# Revit family: DN2_2.0_RT_EC_1FP
name_source: partatom
category: Mechanical Equipment
units: mm (PartAtom-declared; Revit-internal decimal feet)

## family parameters
Always vertical = Yes
Cut with Voids When Loaded = No
OmniClass Number = 23.75.00.00
OmniClass Title = Climate Control (HVAC)
Part Type = Normal
Room Calculation Point = No
Round Connector Dimension = Use Diameter
Shared = No
Work Plane-Based = No

## types (6) — shared parameters
Available Options = Fixed Speed Compressor, Suction Accumlator w/HGRH, Modulating 3-way Valve w/HGRH
Description = Energy Recovery Ventilator
Features (default) = BLDC Variable Speed Compressor, Integrated Refrigeration Controller, Electronic Expansion Valve, Filter Drier, Sight Glass
Manufacturer = Renewaire LLC
Model = DN-2RT-1FP-EC
Nominal Capacity Range = 2T - 10T
Number of Condenser Fans = Qty. 1, EC motor, Direct drive
Refrigerant = R410A
Typical Airflow Range = 375-1,650 CFM
URL = www.renewaire.com

## type names (no varying parameters)
- 2 @ 1.35 kW ea.
- 2 @ 2.70 kW ea.
- 2 @ 3.70 kW ea.
- 2 @ 3HP ea. 208-230V
- 2 @ 3HP ea. 460V
- 2 @ 3HP ea. 575V

## geometry (parser evidence)
native form markers: Sweep x5
no freeform markers — native parametric forms only
